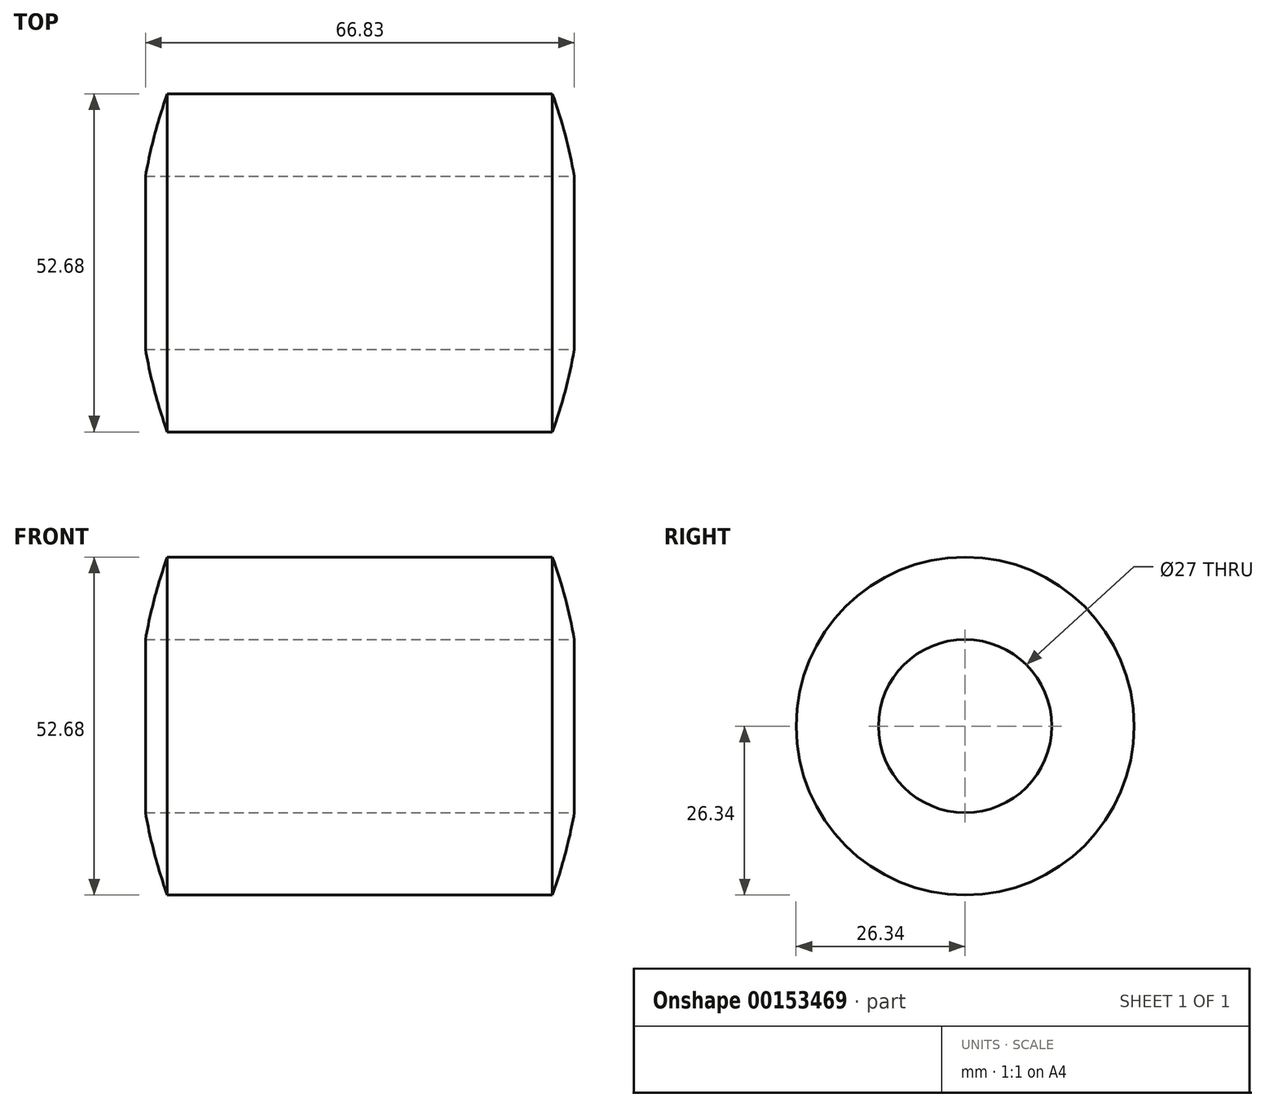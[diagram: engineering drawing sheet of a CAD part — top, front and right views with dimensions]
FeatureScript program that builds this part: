
annotation { "Feature Type Name" : "Feature", "Feature Type Description" : "" }
export const myFeature = defineFeature(function(context is Context, id is Id, definition is map)
    precondition{}
    {
        {
            var Q0;
            Q0=qCreatedBy(makeId("Front.planeOp"),FACE);
            var sketch = newSketch(context, id + "F0", { "sketchPlane" : qUnion([Q0])});
            skArc(sketch, "E0.0", {"start": v(1.79, -26.94) * mm, "mid": v(3.78, -20.6) * mm, "end": v(5.22, -14.1) * mm});
            skLineSegment(sketch, "E1", {"start": v(5.22, 12.9) * mm, "end": v(3.62, 12.9) * mm});
            skLineSegment(sketch, "E2", {"start": v(44.57, -0.6) * mm, "end": v(-32.71, -0.6) * mm});
            skPoint(sketch, "E2.startSnap0", {"position": v(6.4, -0.6) * mm});
            skPoint(sketch, "E2.endSnap0", {"position": v(6.4, -0.6) * mm});
            skArc(sketch, "E3.trimOffspring", {"start": v(5.22, 12.9) * mm, "mid": v(3.7, 19.7) * mm, "end": v(1.57, 26.33) * mm});
            skPoint(sketch, "E4.orphan", {"position": v(0, 12.9) * mm});
            skPoint(sketch, "E5.orphan", {"position": v(0, -14.1) * mm});
            skLineSegment(sketch, "E6", {"start": v(1.57, 26.33) * mm, "end": v(-57.8, 26.33) * mm});
            skPoint(sketch, "E7.orphan", {"position": v(33.45, 26.33) * mm});
            skPoint(sketch, "E8.orphan", {"position": v(33.45, -27.53) * mm});
            skPoint(sketch, "E9.end.orphan", {"position": v(0, 26.93) * mm});
            skPoint(sketch, "E10.end.orphan", {"position": v(0, -26.93) * mm});
            skLineSegment(sketch, "E11", {"start": v(0, 0) * mm, "end": v(0, 12.9) * mm});
            skLineSegment(sketch, "E12", {"start": v(-28.12, 26.33) * mm, "end": v(-28.18, -0.6) * mm});
            skPoint(sketch, "E13.trimOffspring.end.orphan", {"position": v(-57.8, -27.53) * mm});
            skPoint(sketch, "E14.center.orphan", {"position": v(-70.88, 0) * mm});
            skLineSegment(sketch, "E15.trimOffspring", {"start": v(-28.2, -13.85) * mm, "end": v(-28.23, -26.69) * mm});
            skArc(sketch, "E16.MirrorCS", {"start": v(-58.21, -26.94) * mm, "mid": v(-60.19, -20.6) * mm, "end": v(-61.6, -14.1) * mm});
            skLineSegment(sketch, "E17", {"start": v(5.22, -14.1) * mm, "end": v(-61.6, -14.1) * mm});
            skLineSegment(sketch, "E18", {"start": v(1.79, -26.94) * mm, "end": v(-58.21, -26.94) * mm});
            skPoint(sketch, "E19.orphan", {"position": v(-58.26, -26.8) * mm});
            skPoint(sketch, "E20.orphan", {"position": v(-61.63, -13.95) * mm});
            skPoint(sketch, "E21.trimOffspring.end.orphan", {"position": v(0, 26.33) * mm});
            skLineSegment(sketch, "E22.trimOffspring", {"start": v(0, 26.33) * mm, "end": v(0, 39.68) * mm});
            skSolve(sketch);
        }
        {
            var Q0;
            Q0 = qSketchRegion(id + "F0", true);
            var Q1;
            Q1=sQuery(id+"F0.wireOp",EDGE,"E2");
            revolve(context, id + "F1", {"entities" : qUnion([Q0]), "axis" : qUnion([Q1]), "revolveType" : RevolveType.FULL});
        }
    });
